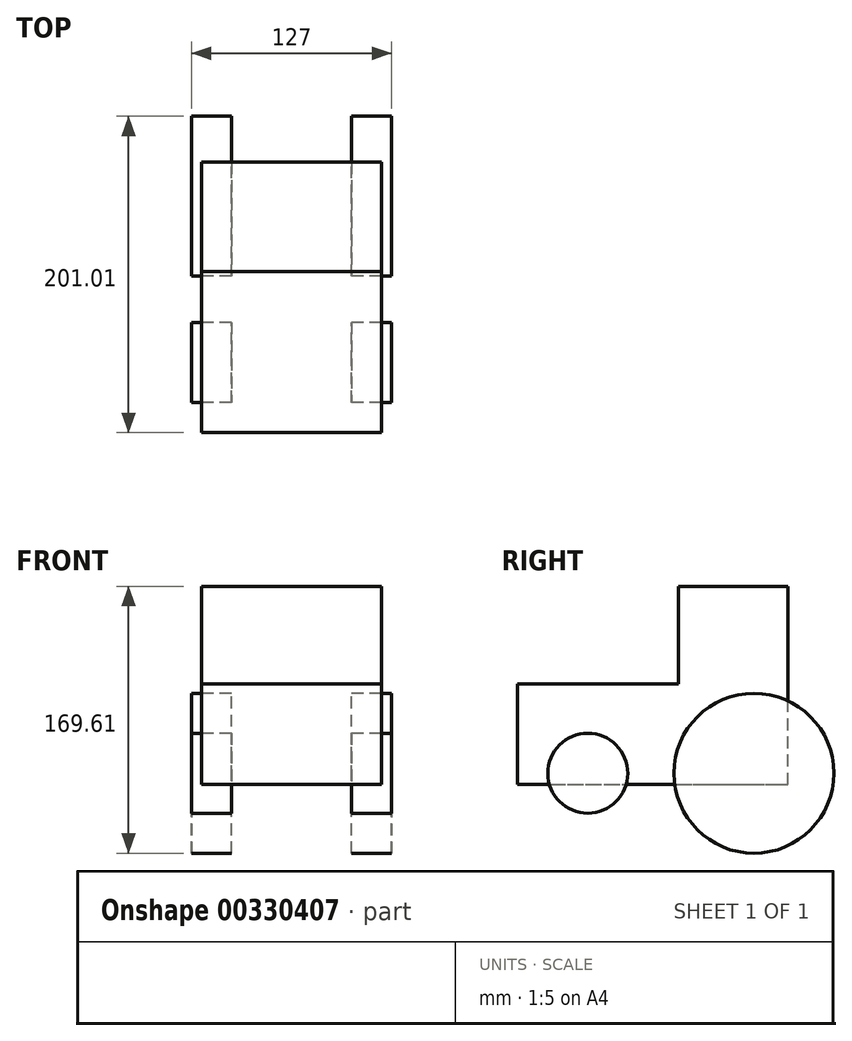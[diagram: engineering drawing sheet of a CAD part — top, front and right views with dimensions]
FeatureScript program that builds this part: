
annotation { "Feature Type Name" : "Feature", "Feature Type Description" : "" }
export const myFeature = defineFeature(function(context is Context, id is Id, definition is map)
    precondition{}
    {
        {
            var Q0;
            Q0=qCreatedBy(makeId("Right.planeOp"),FACE);
            var sketch = newSketch(context, id + "F0", { "sketchPlane" : qUnion([Q0])});
            skCircle(sketch, "E0", {"center": v(-105.5, -34) * mm, "radius": 25.4 * mm});
            skCircle(sketch, "E1", {"center": v(0, -34) * mm, "radius": 50.8 * mm});
            skPoint(sketch, "E2.end.orphan", {"position": v(-105.5, 0) * mm});
            skSolve(sketch);
        }
        {
            var Q0;
            Q0 = qSketchRegion(id + "F0", true);
            extrude(context, id + "F1", {"entities" : qUnion([Q0]), "endBound" : BoundingType.SYMMETRIC, "depth" : 127 * mm});
        }
        {
            var Q0;
            Q0=qCreatedBy(makeId("Right.planeOp"),FACE);
            var sketch = newSketch(context, id + "F2", { "sketchPlane" : qUnion([Q0])});
            skCircle(sketch, "E3", {"center": v(-106.23, -35.13) * mm, "radius": 33.28 * mm});
            skCircle(sketch, "E4", {"center": v(0, -38.27) * mm, "radius": 69.68 * mm});
            skSolve(sketch);
        }
        {
            var Q0;
            Q0 = qSketchRegion(id + "F2", true);
            extrude(context, id + "F3", {"entities" : qUnion([Q0]), "operationType" : NewBodyOperationType.REMOVE, "endBound" : BoundingType.SYMMETRIC, "oppositeDirection" : true, "depth" : 76.2 * mm});
        }
        {
            var Q0;
            Q0=qCreatedBy(makeId("Right.planeOp"),FACE);
            var sketch = newSketch(context, id + "F4", { "sketchPlane" : qUnion([Q0])});
            skLineSegment(sketch, "E5.bottom", {"start": v(-150.21, 22.85) * mm, "end": v(21.7, 22.85) * mm});
            skLineSegment(sketch, "E5.top", {"start": v(-150.21, -41.12) * mm, "end": v(21.7, -41.12) * mm});
            skLineSegment(sketch, "E5.left", {"start": v(-150.21, 22.85) * mm, "end": v(-150.21, -41.12) * mm});
            skLineSegment(sketch, "E5.right", {"start": v(21.7, 22.85) * mm, "end": v(21.7, -41.12) * mm});
            skLineSegment(sketch, "E6.bottom", {"start": v(21.7, -41.12) * mm, "end": v(-47.98, -41.12) * mm});
            skLineSegment(sketch, "E6.top", {"start": v(21.7, 84.82) * mm, "end": v(-47.98, 84.82) * mm});
            skLineSegment(sketch, "E6.left", {"start": v(21.7, -41.12) * mm, "end": v(21.7, 84.82) * mm});
            skLineSegment(sketch, "E6.right", {"start": v(-47.98, -41.12) * mm, "end": v(-47.98, 84.82) * mm});
            skSolve(sketch);
        }
        {
            var Q0;
            Q0 = qSketchRegion(id + "F4", true);
            extrude(context, id + "F5", {"entities" : qUnion([Q0]), "endBound" : BoundingType.SYMMETRIC, "depth" : 114.3 * mm});
        }
    });
